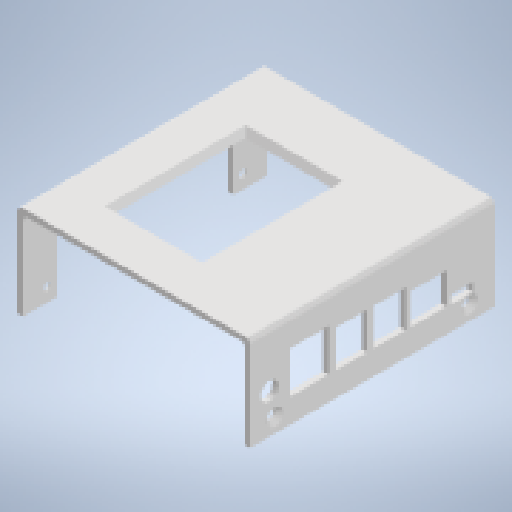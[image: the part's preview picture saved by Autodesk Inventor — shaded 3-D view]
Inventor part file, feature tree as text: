
AUTODESK INVENTOR PART (.ipt)
format: ipt  version: 2024 (Build 280153000, 153)  size: 349,696 bytes
history: native  units: mm
features: reference x18, sketch x4, extrude x4, other x4, plane x2, chamfer x2
ambient origin geometry x8: Origin, YZ Plane, XZ Plane, XY Plane, X Axis, Y Axis, Z Axis, Center Point
bodies: Solid1 (feature_tree)
feature tree (34):
  sketch  "Sketch1"  dims[d0=2.5mm d1=2.5mm]
  plane  "Work Plane1"
  extrude  "Extrusion1"  Depth=2.5mm
  extrude  "Extrusion2"  Depth=2.0mm
  chamfer  "Chamfer1"  Distance=10.0mm
  sketch  "Sketch3"  dims[d6=10.0mm d7=0.0mm d8=2.5mm d9=2.0mm d10=45.0deg]
  plane  "Work Plane2"
  extrude  "Extrusion3"  Depth=2.5mm TaperAngle=45.0deg
  extrude  "Extrusion4"  Depth=2.0mm
  chamfer  "Chamfer2"  Distance=3.5mm
  sketch  "Sketch2"  dims[d2=2.5mm d3=2.0mm d4=10.0mm d5=0.0mm]
  reference  "Reference2"
  sketch  "Sketch4"  dims[d11=10.0mm d12=0.0mm d13=3.5mm d14=3.5mm d15=8.0mm d16=3.5mm d17=3.5mm d18=0.25mm d19=0.25mm d20=0.25mm d21=0.25mm d22=0.25mm d23=0.25mm d24=0.25mm d25=0.25mm d26=0.25mm d27=0.25mm d28=0.25mm d29=0.25mm d30=0.25mm d31=0.25mm d32=0.25mm d33=0.25mm d34=0.5mm d35=0.5mm d36=0.75mm d37=0.75mm d38=10.0mm d39=0.0mm d40=2.0mm d41=2.0mm d42=45.0deg d43=40.0mm d44=39.0mm d45=0.5mm]
  reference  "Reference4"
  reference  "Reference5"
  reference  "Reference6"
  reference  "Reference7"
  reference  "Reference8"
  reference  "Reference9"
  reference  "Reference10"
  reference  "Reference11"
  reference  "Reference12"
  reference  "Reference13"
  reference  "Reference14"
  reference  "Reference15"
  reference  "Reference16"
  reference  "Reference17"
  reference  "Reference18"
  reference  "Reference19"
  reference  "Reference20"
  parser-record x1  (decoder bookkeeping rows leaked as tree rows — omitted from the tree; the rows remain in map.json)
  other  "REV 3 assembly.iam"
  other  "Top3518_3668_A02_3509_A01_0204:1"
  other  "TA07 ELECTRONICS MOUNT REV 3:1"
note: 1 file-system path scrubbed to <path> (originals preserved in map.json)
